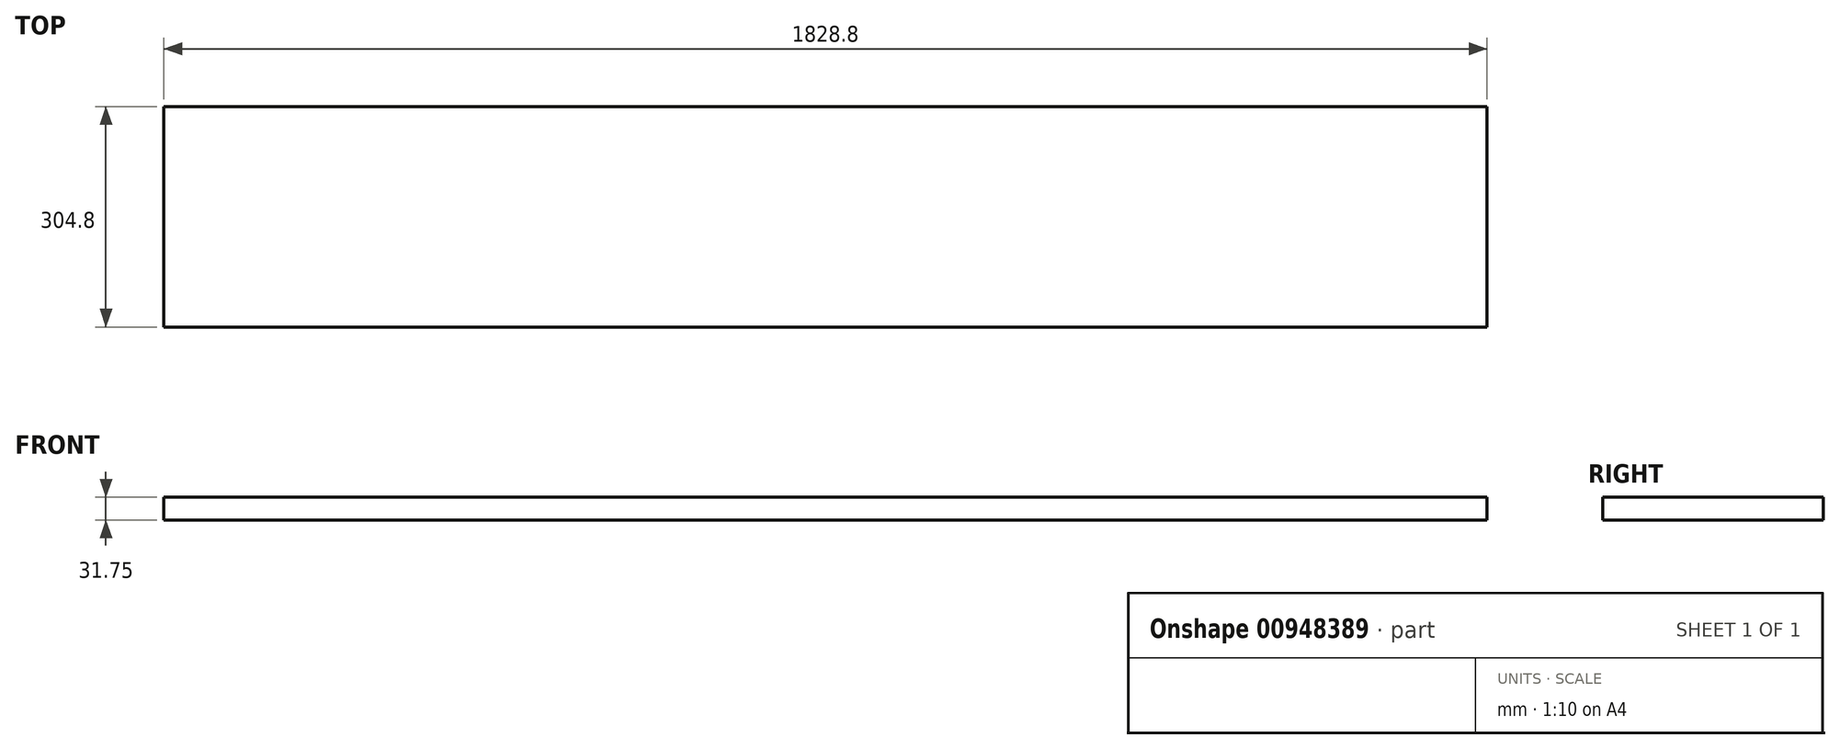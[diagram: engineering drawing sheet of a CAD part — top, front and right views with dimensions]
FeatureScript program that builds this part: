
annotation { "Feature Type Name" : "Feature", "Feature Type Description" : "" }
export const myFeature = defineFeature(function(context is Context, id is Id, definition is map)
    precondition{}
    {
        {
            var Q0;
            Q0=qCreatedBy(makeId("Top.planeOp"),FACE);
            var sketch = newSketch(context, id + "F0", { "sketchPlane" : qUnion([Q0])});
            skLineSegment(sketch, "E0.bottom", {"start": v(-914.4, 152.4) * mm, "end": v(914.4, 152.4) * mm});
            skLineSegment(sketch, "E0.top", {"start": v(-914.4, -152.4) * mm, "end": v(914.4, -152.4) * mm});
            skLineSegment(sketch, "E0.left", {"start": v(-914.4, 152.4) * mm, "end": v(-914.4, -152.4) * mm});
            skLineSegment(sketch, "E0.right", {"start": v(914.4, 152.4) * mm, "end": v(914.4, -152.4) * mm});
            skSolve(sketch);
        }
        {
            var Q0;
            Q0=makeQuery(id+"F0.imprint","IMPRINT",FACE,{"disambiguationData":[TD([[makeQuery(id+"F0.imprint","IMPRINT",EDGE,{"derivedFrom":sQuery(id+"F0.wireOp",EDGE,"E0.bottom")}),-1.0]])]});
            extrude(context, id + "F1", {"entities" : qUnion([Q0]), "depth" : 31.75 * mm, "offsetDistance" : 25.4 * mm});
        }
    });
